# Revit family: N251B
name_source: partatom
category: Sprinklers
revit_build: Autodesk Revit 2018 (Build: 20190510_1515(x64)
units: mm (PartAtom-declared; Revit-internal decimal feet)

## family parameters
Always vertical = Yes
Cut with Voids When Loaded = No
Maintain Annotation Orientation = Yes
OmniClass Number = 23.85.30.21
OmniClass Title = Environmental Detection/Registration
Part Type = Normal
Room Calculation Point = No
Round Connector Dimension = Use Radius
Shared = No
Work Plane-Based = No

## types (1)
- RASCO N25 ESFR
    Coverage = Extended
    Description = BRONZE FINISH
    Diameter = 1"
    K-Factor = 25.2
    Manufacturer = RASCO
    Model = N25 ESFR
    Orifice = Standard
    Orifice Size = 1"
    Pressure Class = Standard
    Pressure Rating = 175 PSI
    RASCO Part # = DB16116391
    RASCO SIN # = RA0912
    Response = Standard
    Temperature Rating = 165 °F

## geometry (parser evidence)
native form markers: Sweep x21
no freeform markers — native parametric forms only
